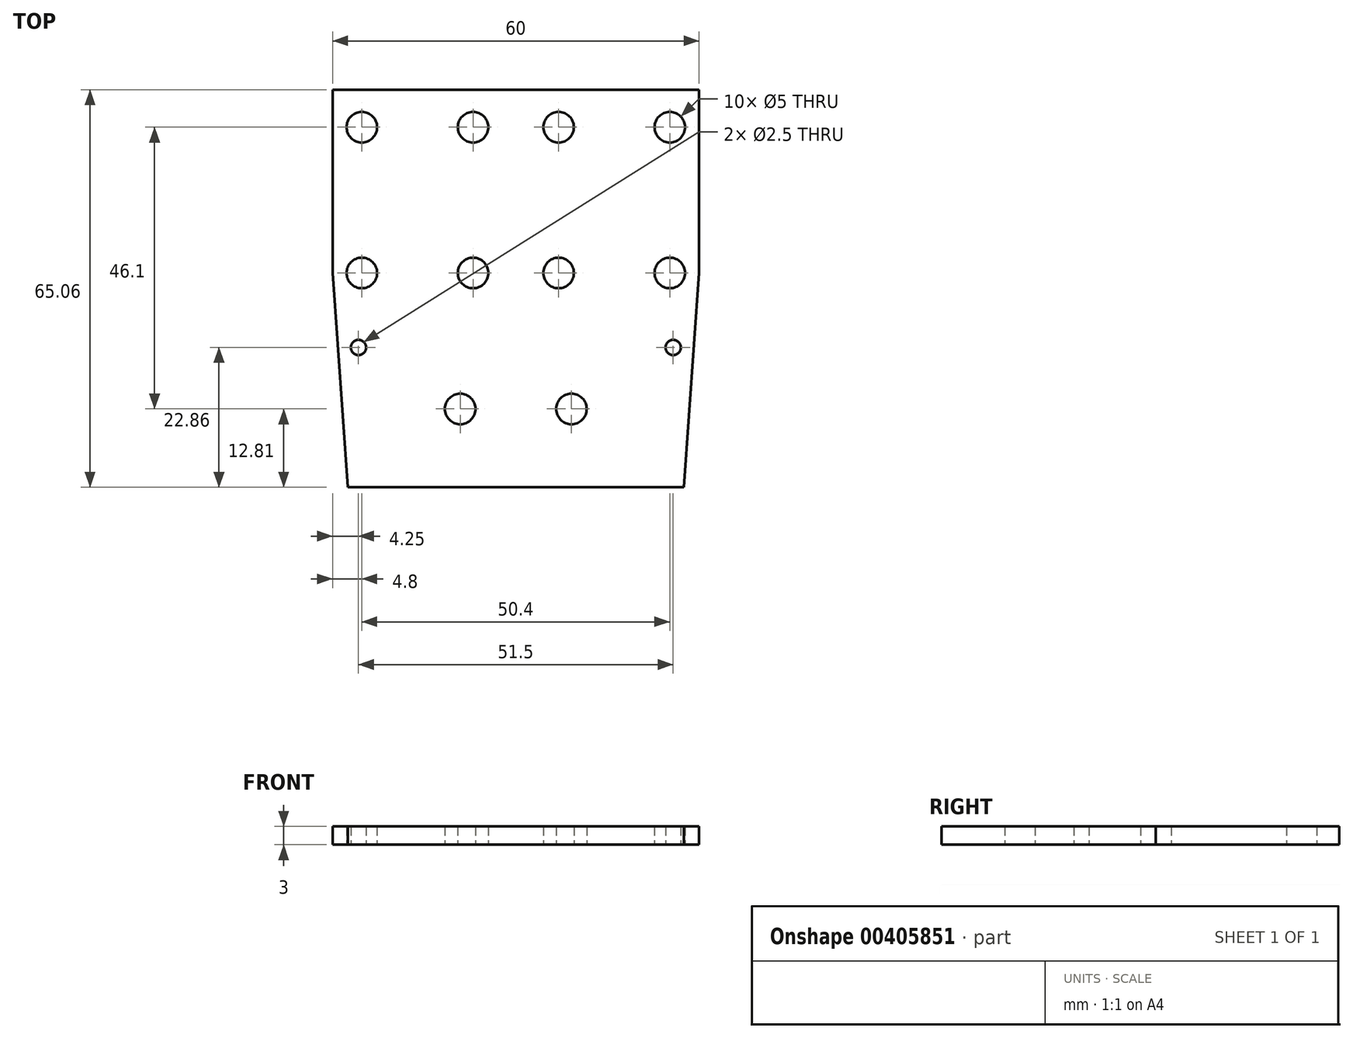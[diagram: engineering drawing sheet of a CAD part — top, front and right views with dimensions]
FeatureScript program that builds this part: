
annotation { "Feature Type Name" : "Feature", "Feature Type Description" : "" }
export const myFeature = defineFeature(function(context is Context, id is Id, definition is map)
    precondition{}
    {
        {
            var Q0;
            Q0=qCreatedBy(makeId("Top.planeOp"),FACE);
            var sketch = newSketch(context, id + "F0", { "sketchPlane" : qUnion([Q0])});
            skCircle(sketch, "E0", {"center": v(-25.2, 23.85) * mm, "radius": 2.5 * mm});
            skCircle(sketch, "E1", {"center": v(-7, 23.85) * mm, "radius": 2.5 * mm});
            skLineSegment(sketch, "E2", {"start": v(-25.2, 23.85) * mm, "end": v(-7, 23.85) * mm, "construction": true});
            skCircle(sketch, "E3", {"center": v(7, 23.85) * mm, "radius": 2.5 * mm});
            skCircle(sketch, "E4", {"center": v(25.2, 23.85) * mm, "radius": 2.5 * mm});
            skLineSegment(sketch, "E5", {"start": v(7, 23.85) * mm, "end": v(25.2, 23.85) * mm, "construction": true});
            skCircle(sketch, "E6", {"center": v(-25.2, 0) * mm, "radius": 2.5 * mm});
            skLineSegment(sketch, "E7", {"start": v(-25.2, 23.85) * mm, "end": v(-25.2, 0) * mm, "construction": true});
            skCircle(sketch, "E8", {"center": v(-7, 0) * mm, "radius": 2.5 * mm});
            skLineSegment(sketch, "E9", {"start": v(-25.2, 0) * mm, "end": v(-7, 0) * mm, "construction": true});
            skCircle(sketch, "E10", {"center": v(7, 0) * mm, "radius": 2.5 * mm});
            skCircle(sketch, "E11", {"center": v(25.2, 0) * mm, "radius": 2.5 * mm});
            skLineSegment(sketch, "E12", {"start": v(7, 0) * mm, "end": v(25.2, 0) * mm, "construction": true});
            skLineSegment(sketch, "E13", {"start": v(25.2, 23.85) * mm, "end": v(25.2, 0) * mm, "construction": true});
            skCircle(sketch, "E14", {"center": v(-9.1, -22.25) * mm, "radius": 2.5 * mm});
            skCircle(sketch, "E15", {"center": v(9.1, -22.25) * mm, "radius": 2.5 * mm});
            skLineSegment(sketch, "E16", {"start": v(-9.1, -22.25) * mm, "end": v(9.1, -22.25) * mm, "construction": true});
            skLineSegment(sketch, "E17", {"start": v(-7, 23.85) * mm, "end": v(7, 23.85) * mm, "construction": true});
            skLineSegment(sketch, "E18", {"start": v(7, 0) * mm, "end": v(-7, 0) * mm, "construction": true});
            skLineSegment(sketch, "E19", {"start": v(0, -22.25) * mm, "end": v(0, 0) * mm, "construction": true});
            skLineSegment(sketch, "E20", {"start": v(-30, 30) * mm, "end": v(30, 30) * mm});
            skLineSegment(sketch, "E21", {"start": v(30, 30) * mm, "end": v(30, 0) * mm});
            skLineSegment(sketch, "E22", {"start": v(30, 0) * mm, "end": v(27.5, -35.06) * mm});
            skLineSegment(sketch, "E23", {"start": v(27.5, -35.06) * mm, "end": v(-27.5, -35.06) * mm});
            skLineSegment(sketch, "E24", {"start": v(-27.5, -35.06) * mm, "end": v(-30, 0) * mm});
            skLineSegment(sketch, "E25", {"start": v(-30, 0) * mm, "end": v(-30, 30) * mm});
            skLineSegment(sketch, "E26", {"start": v(0, 23.85) * mm, "end": v(0, 30) * mm, "construction": true});
            skCircle(sketch, "E27", {"center": v(25.75, -12.2) * mm, "radius": 1.25 * mm});
            skCircle(sketch, "E28", {"center": v(-25.75, -12.2) * mm, "radius": 1.25 * mm});
            skLineSegment(sketch, "E29", {"start": v(25.75, -12.2) * mm, "end": v(-25.75, -12.2) * mm, "construction": true});
            skLineSegment(sketch, "E30", {"start": v(0, -12.2) * mm, "end": v(0, -35.06) * mm, "construction": true});
            skSolve(sketch);
        }
        {
            var Q0;
            Q0=makeQuery(id+"F0.imprint","IMPRINT",FACE,{"disambiguationData":[TD([[makeQuery(id+"F0.imprint","IMPRINT",EDGE,{"derivedFrom":sQuery(id+"F0.wireOp",EDGE,"E0")}),-1.0]])]});
            extrude(context, id + "F1", {"entities" : qUnion([Q0]), "depth" : 3 * mm, "offsetDistance" : 25 * mm});
        }
    });
